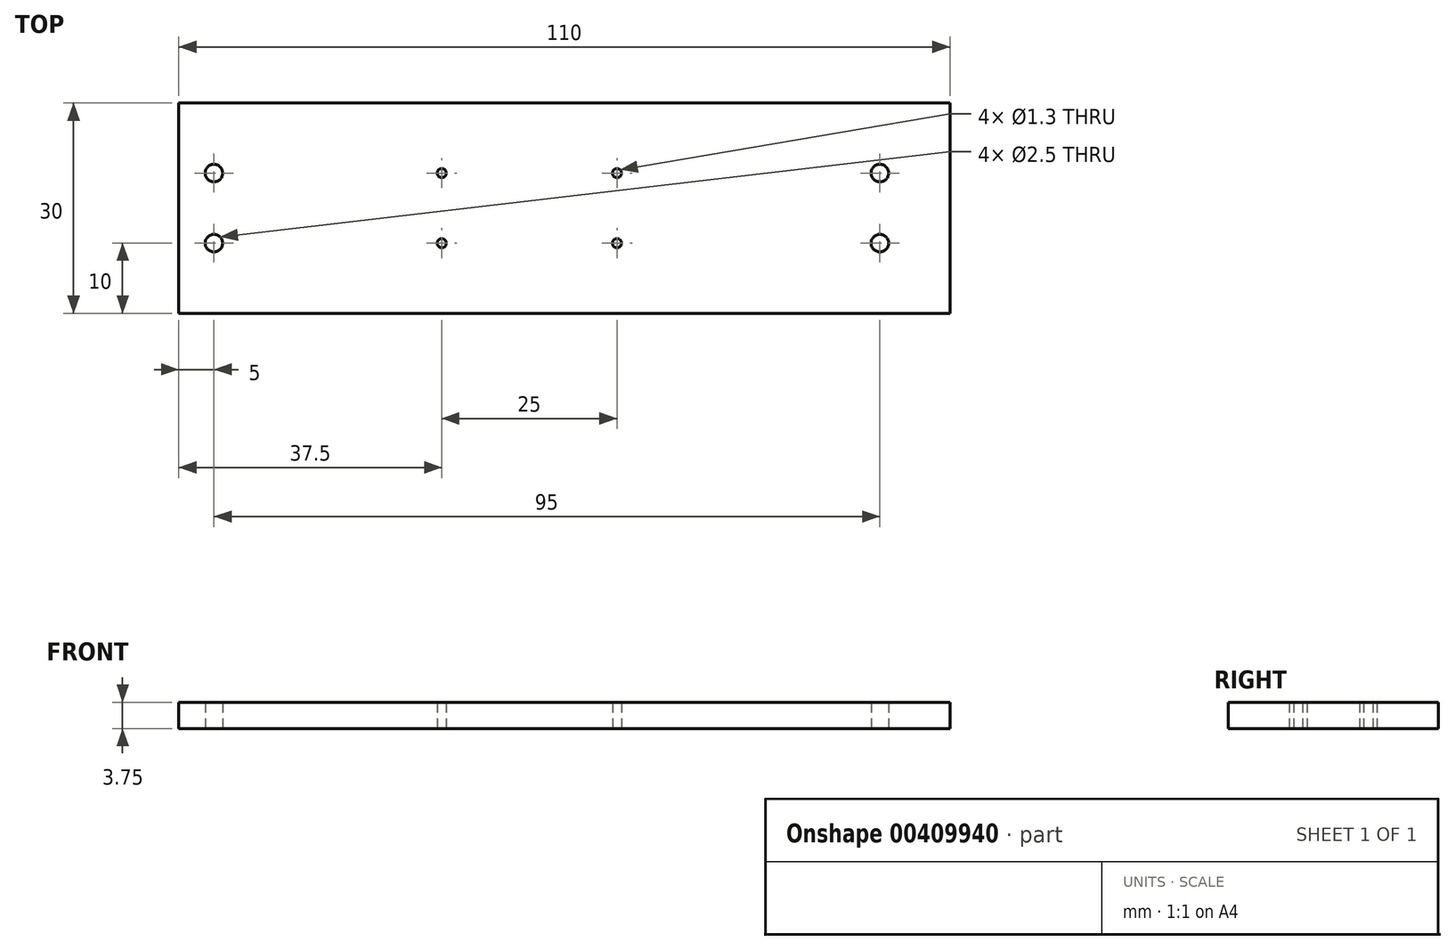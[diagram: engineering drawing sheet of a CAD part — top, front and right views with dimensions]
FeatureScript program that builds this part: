
annotation { "Feature Type Name" : "Feature", "Feature Type Description" : "" }
export const myFeature = defineFeature(function(context is Context, id is Id, definition is map)
    precondition{}
    {
        {
            var Q0;
            Q0=qCreatedBy(makeId("Top.planeOp"),FACE);
            var sketch = newSketch(context, id + "F0", { "sketchPlane" : qUnion([Q0])});
            skLineSegment(sketch, "E0.bottom", {"start": v(0, 0) * mm, "end": v(110, 0) * mm});
            skLineSegment(sketch, "E0.top", {"start": v(0, 30) * mm, "end": v(110, 30) * mm});
            skLineSegment(sketch, "E0.left", {"start": v(0, 0) * mm, "end": v(0, 30) * mm});
            skLineSegment(sketch, "E0.right", {"start": v(110, 0) * mm, "end": v(110, 30) * mm});
            skCircle(sketch, "E1", {"center": v(5, 20) * mm, "radius": 1.25 * mm});
            skCircle(sketch, "E2", {"center": v(5, 10) * mm, "radius": 1.25 * mm});
            skCircle(sketch, "E3", {"center": v(100, 20) * mm, "radius": 1.25 * mm});
            skCircle(sketch, "E4", {"center": v(100, 10) * mm, "radius": 1.25 * mm});
            skCircle(sketch, "E5", {"center": v(37.5, 20) * mm, "radius": 0.65 * mm});
            skCircle(sketch, "E6", {"center": v(37.5, 10) * mm, "radius": 0.65 * mm});
            skCircle(sketch, "E7", {"center": v(62.5, 20) * mm, "radius": 0.65 * mm});
            skCircle(sketch, "E8", {"center": v(62.5, 10) * mm, "radius": 0.65 * mm});
            skSolve(sketch);
        }
        {
            var Q0;
            Q0=makeQuery(id+"F0.imprint","IMPRINT",FACE,{"disambiguationData":[TD([[makeQuery(id+"F0.imprint","IMPRINT",EDGE,{"derivedFrom":sQuery(id+"F0.wireOp",EDGE,"E0.bottom")}),1.0]])]});
            extrude(context, id + "F1", {"entities" : qUnion([Q0]), "depth" : 3.75 * mm});
        }
    });
